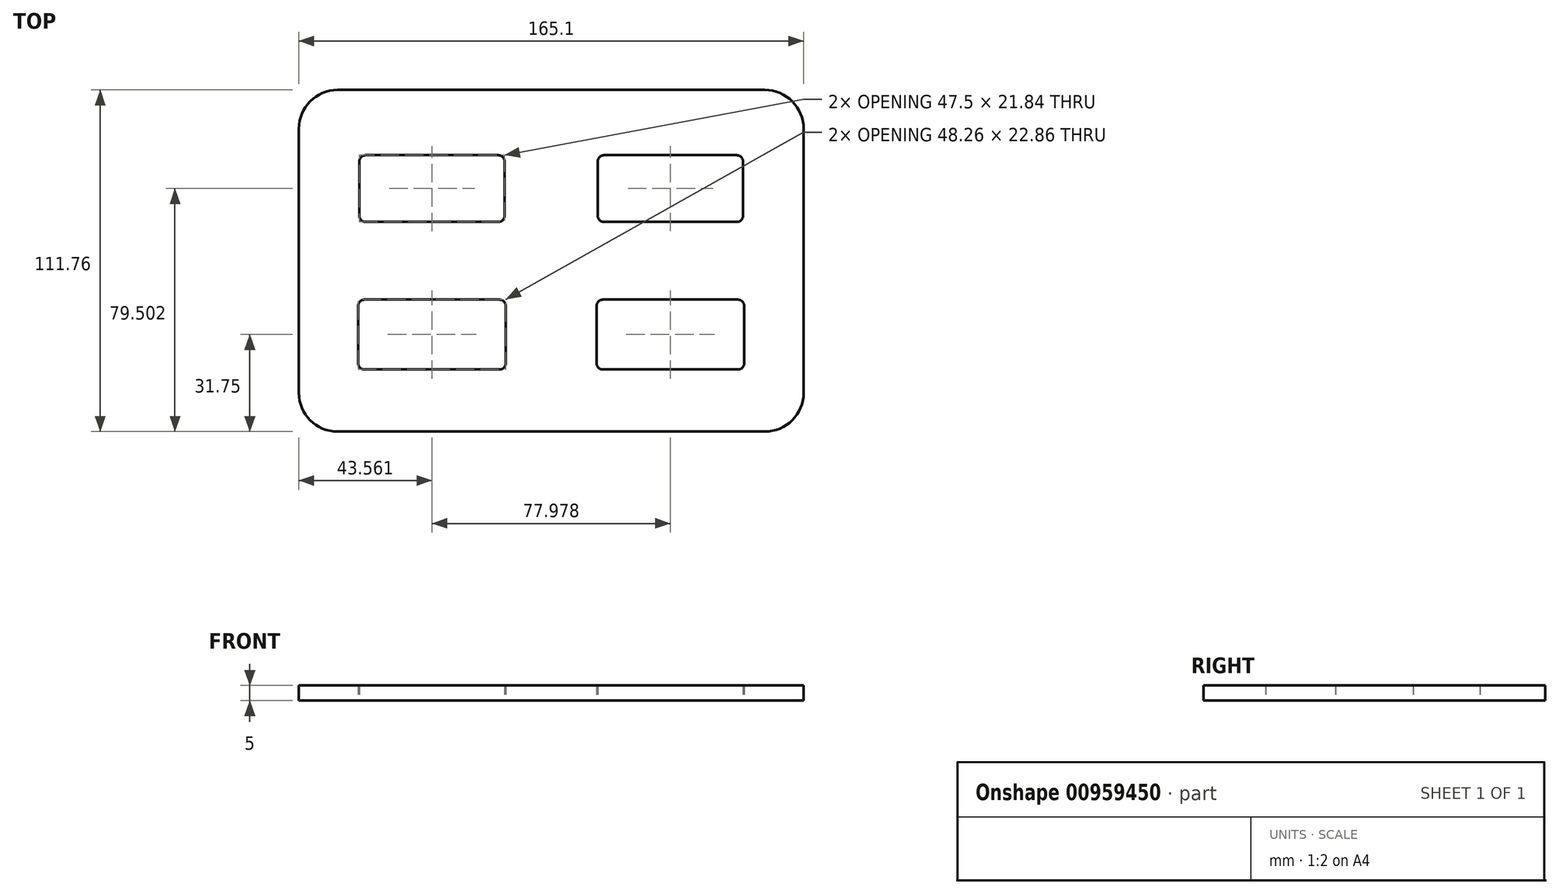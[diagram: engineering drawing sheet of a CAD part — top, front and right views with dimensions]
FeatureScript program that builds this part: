
annotation { "Feature Type Name" : "Feature", "Feature Type Description" : "" }
export const myFeature = defineFeature(function(context is Context, id is Id, definition is map)
    precondition{}
    {
        {
            var Q0;
            Q0=qCreatedBy(makeId("Top.planeOp"),FACE);
            var sketch = newSketch(context, id + "F0", { "sketchPlane" : qUnion([Q0])});
            skLineSegment(sketch, "E0.bottom", {"start": v(12.7, 0) * mm, "end": v(152.4, 0) * mm});
            skLineSegment(sketch, "E0.top", {"start": v(12.7, 111.76) * mm, "end": v(152.4, 111.76) * mm});
            skLineSegment(sketch, "E0.left", {"start": v(0, 12.7) * mm, "end": v(0, 99.06) * mm});
            skLineSegment(sketch, "E0.right", {"start": v(165.1, 12.7) * mm, "end": v(165.1, 99.06) * mm});
            skLineSegment(sketch, "E1.bottom", {"start": v(21.84, 90.42) * mm, "end": v(65.28, 90.42) * mm});
            skLineSegment(sketch, "E1.top", {"start": v(21.84, 68.58) * mm, "end": v(65.28, 68.58) * mm});
            skLineSegment(sketch, "E1.left", {"start": v(19.81, 88.4) * mm, "end": v(19.81, 70.61) * mm});
            skLineSegment(sketch, "E1.right", {"start": v(67.31, 88.4) * mm, "end": v(67.31, 70.61) * mm});
            skLineSegment(sketch, "E2", {"start": v(165.1, 111.76) * mm, "end": v(82.55, 111.76) * mm, "construction": true});
            skLineSegment(sketch, "E3", {"start": v(82.55, 111.76) * mm, "end": v(82.55, 0) * mm, "construction": true});
            skLineSegment(sketch, "E4.MirrorCS", {"start": v(97.8, 88.4) * mm, "end": v(97.8, 70.61) * mm});
            skLineSegment(sketch, "E5.MirrorCS", {"start": v(143.26, 90.42) * mm, "end": v(99.82, 90.42) * mm});
            skLineSegment(sketch, "E6.MirrorCS", {"start": v(143.26, 68.58) * mm, "end": v(99.82, 68.58) * mm});
            skLineSegment(sketch, "E7.MirrorCS", {"start": v(145.29, 88.4) * mm, "end": v(145.29, 70.61) * mm});
            skLineSegment(sketch, "E8", {"start": v(0, 55.88) * mm, "end": v(165.1, 55.88) * mm, "construction": true});
            skLineSegment(sketch, "E9", {"start": v(67.31, 79.5) * mm, "end": v(82.55, 79.5) * mm, "construction": true});
            skLineSegment(sketch, "E10", {"start": v(43.56, 68.58) * mm, "end": v(43.56, 55.88) * mm, "construction": true});
            skPoint(sketch, "E11.visualSharp", {"position": v(19.81, 90.42) * mm});
            skArc(sketch, "E11.filletArc", {"start": v(21.84, 90.42) * mm, "mid": v(20.4, 89.83) * mm, "end": v(19.81, 88.4) * mm});
            skPoint(sketch, "E12.visualSharp", {"position": v(67.31, 90.42) * mm});
            skArc(sketch, "E12.filletArc", {"start": v(67.31, 88.4) * mm, "mid": v(66.71, 89.83) * mm, "end": v(65.28, 90.42) * mm});
            skPoint(sketch, "E13.visualSharp", {"position": v(67.31, 68.58) * mm});
            skArc(sketch, "E13.filletArc", {"start": v(65.28, 68.58) * mm, "mid": v(66.71, 69.18) * mm, "end": v(67.31, 70.61) * mm});
            skPoint(sketch, "E14.visualSharp", {"position": v(19.81, 68.58) * mm});
            skArc(sketch, "E14.filletArc", {"start": v(19.81, 70.61) * mm, "mid": v(20.4, 69.18) * mm, "end": v(21.84, 68.58) * mm});
            skPoint(sketch, "E15.visualSharp", {"position": v(97.8, 68.58) * mm});
            skArc(sketch, "E15.filletArc", {"start": v(97.79, 70.61) * mm, "mid": v(98.39, 69.18) * mm, "end": v(99.82, 68.58) * mm});
            skPoint(sketch, "E16.visualSharp", {"position": v(97.8, 90.42) * mm});
            skArc(sketch, "E16.filletArc", {"start": v(99.82, 90.42) * mm, "mid": v(98.39, 89.83) * mm, "end": v(97.79, 88.4) * mm});
            skPoint(sketch, "E17.visualSharp", {"position": v(145.29, 90.42) * mm});
            skArc(sketch, "E17.filletArc", {"start": v(145.29, 88.4) * mm, "mid": v(144.7, 89.83) * mm, "end": v(143.26, 90.42) * mm});
            skPoint(sketch, "E18.visualSharp", {"position": v(145.29, 68.58) * mm});
            skArc(sketch, "E18.filletArc", {"start": v(143.26, 68.58) * mm, "mid": v(144.7, 69.18) * mm, "end": v(145.29, 70.61) * mm});
            skPoint(sketch, "E19.visualSharp", {"position": v(0, 111.76) * mm});
            skArc(sketch, "E19.filletArc", {"start": v(12.7, 111.76) * mm, "mid": v(3.72, 108.04) * mm, "end": v(0, 99.06) * mm});
            skPoint(sketch, "E20.visualSharp", {"position": v(165.1, 111.76) * mm});
            skArc(sketch, "E20.filletArc", {"start": v(165.1, 99.06) * mm, "mid": v(161.38, 108.04) * mm, "end": v(152.4, 111.76) * mm});
            skPoint(sketch, "E21.visualSharp", {"position": v(0, 0) * mm});
            skArc(sketch, "E21.filletArc", {"start": v(0, 12.7) * mm, "mid": v(3.72, 3.72) * mm, "end": v(12.7, 0) * mm});
            skPoint(sketch, "E22.visualSharp", {"position": v(165.1, 0) * mm});
            skArc(sketch, "E22.filletArc", {"start": v(152.4, 0) * mm, "mid": v(161.38, 3.72) * mm, "end": v(165.1, 12.7) * mm});
            skLineSegment(sketch, "E23.bottom", {"start": v(21.46, 43.18) * mm, "end": v(65.66, 43.18) * mm});
            skLineSegment(sketch, "E23.top", {"start": v(21.46, 20.32) * mm, "end": v(65.66, 20.32) * mm});
            skLineSegment(sketch, "E23.left", {"start": v(19.43, 41.15) * mm, "end": v(19.43, 22.35) * mm});
            skLineSegment(sketch, "E23.right", {"start": v(67.7, 41.15) * mm, "end": v(67.7, 22.35) * mm});
            skLineSegment(sketch, "E24", {"start": v(43.56, 55.88) * mm, "end": v(43.56, 43.18) * mm, "construction": true});
            skLineSegment(sketch, "E25.MirrorCS", {"start": v(143.64, 20.32) * mm, "end": v(99.44, 20.32) * mm});
            skLineSegment(sketch, "E26.MirrorCS", {"start": v(97.4, 41.15) * mm, "end": v(97.4, 22.35) * mm});
            skLineSegment(sketch, "E27.MirrorCS", {"start": v(145.67, 41.15) * mm, "end": v(145.67, 22.35) * mm});
            skLineSegment(sketch, "E28.MirrorCS", {"start": v(143.64, 43.18) * mm, "end": v(99.44, 43.18) * mm});
            skPoint(sketch, "E29.visualSharp", {"position": v(19.43, 43.18) * mm});
            skArc(sketch, "E29.filletArc", {"start": v(21.46, 43.18) * mm, "mid": v(20.03, 42.58) * mm, "end": v(19.43, 41.15) * mm});
            skPoint(sketch, "E30.visualSharp", {"position": v(19.43, 20.32) * mm});
            skArc(sketch, "E30.filletArc", {"start": v(19.43, 22.35) * mm, "mid": v(20.03, 20.92) * mm, "end": v(21.46, 20.32) * mm});
            skPoint(sketch, "E31.visualSharp", {"position": v(67.7, 43.18) * mm});
            skArc(sketch, "E31.filletArc", {"start": v(67.7, 41.15) * mm, "mid": v(67.1, 42.58) * mm, "end": v(65.66, 43.18) * mm});
            skPoint(sketch, "E32.visualSharp", {"position": v(67.7, 20.32) * mm});
            skArc(sketch, "E32.filletArc", {"start": v(65.66, 20.32) * mm, "mid": v(67.1, 20.92) * mm, "end": v(67.7, 22.35) * mm});
            skPoint(sketch, "E33.visualSharp", {"position": v(97.4, 43.18) * mm});
            skArc(sketch, "E33.filletArc", {"start": v(99.44, 43.18) * mm, "mid": v(98, 42.58) * mm, "end": v(97.4, 41.15) * mm});
            skPoint(sketch, "E34.visualSharp", {"position": v(97.4, 20.32) * mm});
            skArc(sketch, "E34.filletArc", {"start": v(97.4, 22.35) * mm, "mid": v(98, 20.92) * mm, "end": v(99.44, 20.32) * mm});
            skPoint(sketch, "E35.visualSharp", {"position": v(145.67, 43.18) * mm});
            skArc(sketch, "E35.filletArc", {"start": v(145.67, 41.15) * mm, "mid": v(145.07, 42.58) * mm, "end": v(143.64, 43.18) * mm});
            skPoint(sketch, "E36.visualSharp", {"position": v(145.67, 20.32) * mm});
            skArc(sketch, "E36.filletArc", {"start": v(143.64, 20.32) * mm, "mid": v(145.07, 20.92) * mm, "end": v(145.67, 22.35) * mm});
            skSolve(sketch);
        }
        {
            var Q0;
            Q0 = qSketchRegion(id + "F0", true);
            extrude(context, id + "F1", {"entities" : qUnion([Q0]), "depth" : 5 * mm, "offsetDistance" : 25 * mm});
        }
    });
